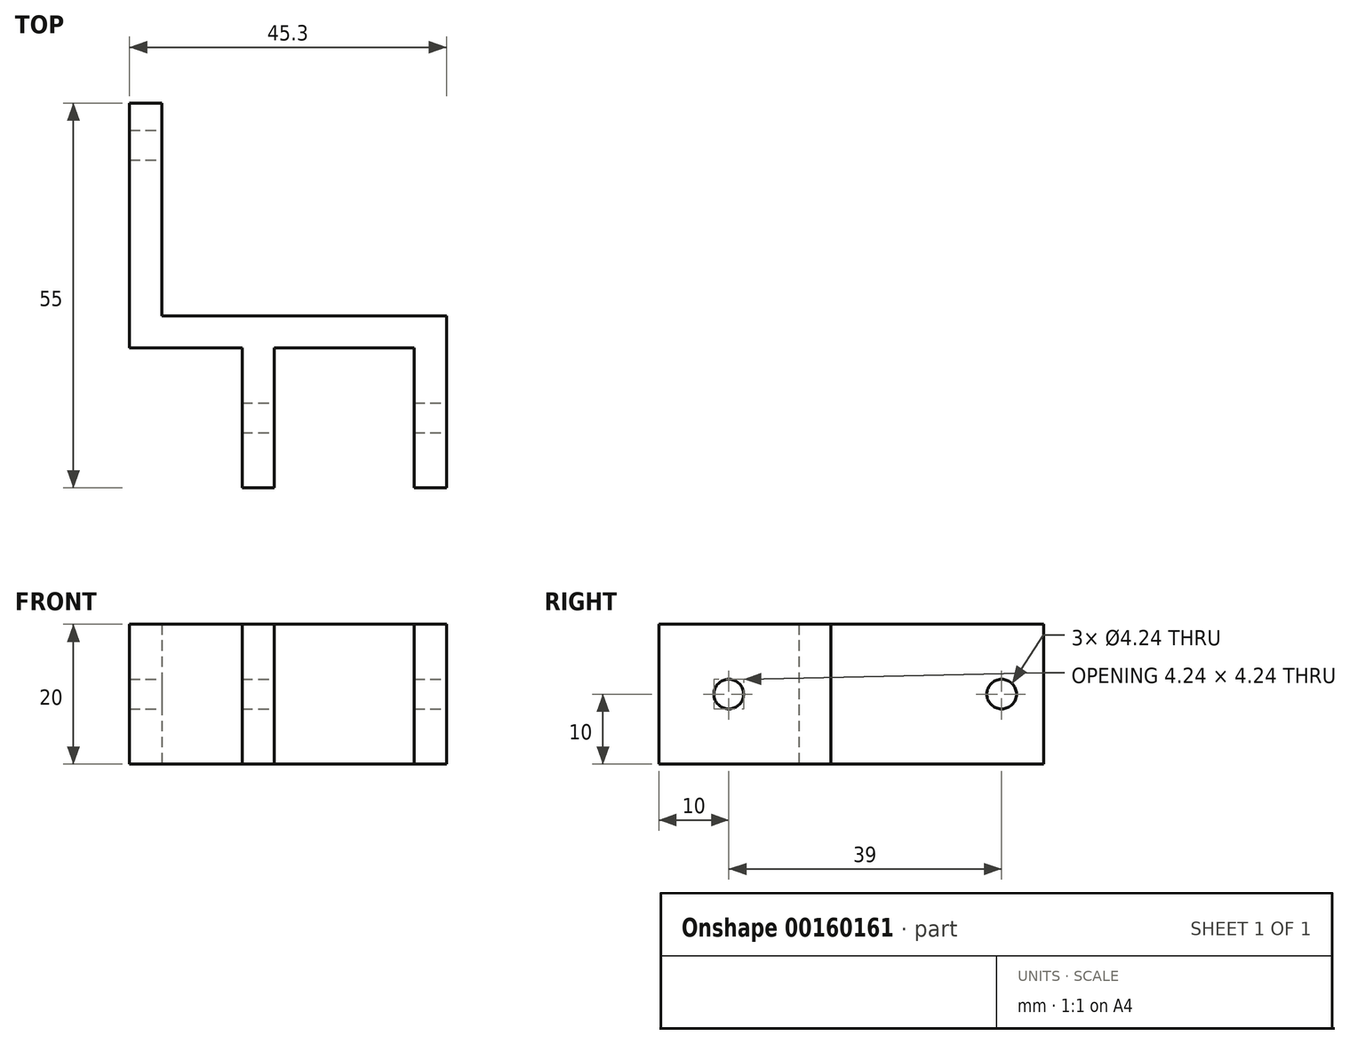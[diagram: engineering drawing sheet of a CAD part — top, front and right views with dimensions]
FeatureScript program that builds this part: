
annotation { "Feature Type Name" : "Feature", "Feature Type Description" : "" }
export const myFeature = defineFeature(function(context is Context, id is Id, definition is map)
    precondition{}
    {
        {
            var Q0;
            Q0=qCreatedBy(makeId("Top.planeOp"),FACE);
            var sketch = newSketch(context, id + "F0", { "sketchPlane" : qUnion([Q0])});
            skLineSegment(sketch, "E0", {"start": v(24.6, 0) * mm, "end": v(24.6, 24.6) * mm});
            skLineSegment(sketch, "E1", {"start": v(24.6, 24.6) * mm, "end": v(-16.1, 24.6) * mm});
            skLineSegment(sketch, "E2", {"start": v(-16.1, 24.6) * mm, "end": v(-16.1, 55) * mm});
            skLineSegment(sketch, "E3", {"start": v(-16.1, 55) * mm, "end": v(-20.7, 55) * mm});
            skLineSegment(sketch, "E4", {"start": v(-20.7, 55) * mm, "end": v(-20.7, 20) * mm});
            skLineSegment(sketch, "E5", {"start": v(-20.7, 20) * mm, "end": v(-4.6, 20) * mm});
            skLineSegment(sketch, "E6", {"start": v(-4.6, 20) * mm, "end": v(-4.6, 0) * mm});
            skLineSegment(sketch, "E7", {"start": v(-4.6, 0) * mm, "end": v(0, 0) * mm});
            skLineSegment(sketch, "E8", {"start": v(0, 0) * mm, "end": v(0, 20) * mm});
            skLineSegment(sketch, "E9", {"start": v(0, 20) * mm, "end": v(20, 20) * mm});
            skLineSegment(sketch, "E10", {"start": v(20, 20) * mm, "end": v(20, 0) * mm});
            skLineSegment(sketch, "E11", {"start": v(20, 0) * mm, "end": v(24.6, 0) * mm});
            skPoint(sketch, "E12", {"position": v(0, 0) * mm});
            skSolve(sketch);
        }
        {
            var Q0;
            Q0 = qSketchRegion(id + "F0", true);
            extrude(context, id + "F1", {"entities" : qUnion([Q0]), "endBound" : BoundingType.SYMMETRIC, "depth" : 20 * mm});
        }
        {
            var Q0;
            Q0=makeQuery(id+"F1.opExtrude","SWEPT_FACE",FACE,{"disambiguationData":[OSD([sQuery(id+"F0.wireOp",EDGE,"E2")])]});
            var sketch = newSketch(context, id + "F2", { "sketchPlane" : qUnion([Q0])});
            skCircle(sketch, "E13", {"center": v(49, 0) * mm, "radius": 2.12 * mm});
            skCircle(sketch, "E14", {"center": v(10, 0) * mm, "radius": 2.12 * mm});
            skSolve(sketch);
        }
        {
            var Q0;
            Q0 = qSketchRegion(id + "F2", true);
            extrude(context, id + "F3", {"entities" : qUnion([Q0]), "operationType" : NewBodyOperationType.REMOVE, "endBound" : BoundingType.THROUGH_ALL, "oppositeDirection" : true, "depth" : 25.4 * mm, "hasSecondDirection" : true, "secondDirectionBound" : SecondDirectionBoundingType.THROUGH_ALL, "secondDirectionOppositeDirection" : false, "secondDirectionDepth" : 25.4 * mm});
        }
    });
